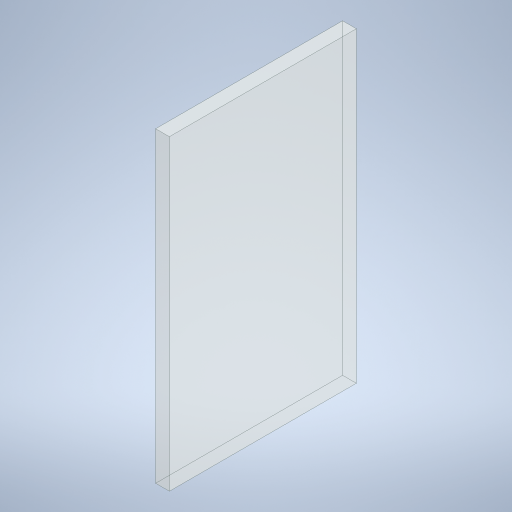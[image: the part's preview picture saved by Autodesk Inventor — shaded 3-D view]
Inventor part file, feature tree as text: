
AUTODESK INVENTOR PART (.ipt)
format: ipt  version: 2024 (Build 280153000, 153)  size: 241,152 bytes
history: native  units: in
note: dims shown in document units (in); Inventor stores cm internally (conversion verified against a paired STEP export)
features: extrude x1, sketch x1
ambient origin geometry x8: Origin, YZ Plane, XZ Plane, XY Plane, X Axis, Y Axis, Z Axis, Center Point
bodies: Solid1 (feature_tree)
feature tree (2):
  extrude  "Extrusion1"  Depth=78.0in
  sketch  "Sketch1"  dims[d2=47.5in d3=78.0in d4=3.5in d5=0.0in]
